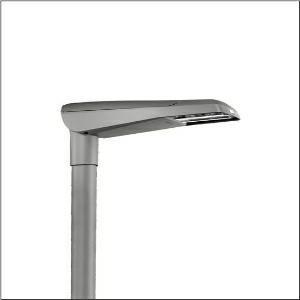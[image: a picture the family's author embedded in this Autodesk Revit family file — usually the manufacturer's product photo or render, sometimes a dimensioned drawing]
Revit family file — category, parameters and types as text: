
# Revit family: streetlight_sl_11_iq_micro___st1_0a_5xc1m51f08ce_5929
name_source: partatom
category: Lighting Fixtures
units: mm (PartAtom-declared; Revit-internal decimal feet)

## family parameters
Cut with Voids When Loaded = No
Host = Face
Light Source = No
Part Type = Normal
Room Calculation Point = No
Round Connector Dimension = Use Diameter
Shared = No

## types (1)
- --- (1 x LED, 1820 lm, 12.6 W, 3000K)
    Apparent Load = 13 VA
    CIE Flux Codes = 33 66 96 100 100
    Color Rendering = 70
    Color Temperature = 3000K
    Default Elevation = 1800 mm
    Description = Streetlight SL 11 iQ micro, mast luminaire, primary light control with 3 zone facetted reflector, of plastic, silver coated, highly specular, primary optical cover: cover, of PMMA, transparent, light distribution: ST1.0a, light emission: direct distribution, primary light characteristic: asymmetric, installation type: post-top, side-entry, lamps: LED, High Power LED, rated values: 1.820lm | 12,6W | 144,4lm/W (begin service life); end service life: 1.820lm | 12,9W; at 50% lumin. flux: 910lm | 6,8W | 133,8lm/W, colour temperature: 3000K, colour rendering: CRI > 70, light colour: 730, light setting 1 begin service life: 100% | 1.820lm | 12,6W | 144,4lm/W | 3.000K, light setting 1 end service life: 12,9W, further light settings possible, control: optimised constant luminous flux control (CLO 2.0), Desk-Remote (wireless, voltage-free reading and setting of iQ features in the workshop via application-optimized NFC function/RFID function), Light-Fading, Smart-Wire, Night-Set, Lumen-Switch, Temp-Guard, Auto-Match, Street-Remote, with cable H07RN-F 5x 1.5mm², mains connection: 230..240V, AC, 50/60Hz, connection cable pre-assembled, cable length: 5,5m, luminaire housing, of diecast aluminium, powder-coated, Siteco® metallic grey (DB 702S), please order mast flange separately, inclination adjustable without tools: 0°, 5°, 10°, 15° (post-top) | 0°, -5°, -10°, -15° (side-entry), sealing non-destructively replaceable, multi-level sealing system, length: 600mm, width: 174mm, height: 116mm, mast flange for spigot size: 42mm (side-entry): 5XC10008XM4, 60/48mm (side-entry/post-top): 5XC10108XM2, 76/60mm (side-entry/post-top): 5XC10108XM1, equipment: standard, protection rating (complete): IP66, insulation class (complete): insulation class II (safety insulation), certification: CE, ENEC, ENEC+, VDE, impact resistance: IK10, permissible operating ambient temperature for outdoor applications: -25..+50°C, standard-compliant lighting for roads and squares, Environmental Product Declaration (EPD) tested and certified by an independent institute, packaging unit: 1 piece

Light Distribution: ST1.0a
    Height = 116 mm
    Lamp = 1 x LED
    Lamp Light Flux = 1820 lm
    Lamp Power = 12.6 W
    Lamp count = 1
    Length = 600 mm
    Luminous efficacy = 144 lm/W
    Manufacturer = Siteco
    ModVariant = No
    Model = 5XC1M51F08CE
    Number of Poles = 1
    OnlyDefault = Yes
    Power Factor = 1
    Product Name = Streetlight SL 11 iQ micro | ST1.0a
    Product group = mast luminaire | pylon top
    ProductGroupID = 6100
    Protection Class = Protection class II
    Protection Degree = IP 66
    RLX_Detail_Level = 1
    RLX_Emergency_Light_Flux = 0 lm
    RLX_Emergency_Type = 0
    RLX_Emergency_Type_DB = No
    RlxData = <blob elided: 26245 chars, md5=86f6f62d>
    Socket = socket
    Standby Power = 0 W
    System Light Flux = 1820 lm
    System Power = 13 W
    Type Comments = factory setting: luminous flux: 100 % | dim-lin: 254 | 229 mA
    Type Image = l_1006566.jpg
    URL = http://relux.com
    VarID = @adj_020465
    Voltage = 0 V
    Weight = 0.00 kg
    Width = 174 mm

## geometry (parser evidence)
native form markers: Blend x4, Sweep x12
no freeform markers — native parametric forms only
